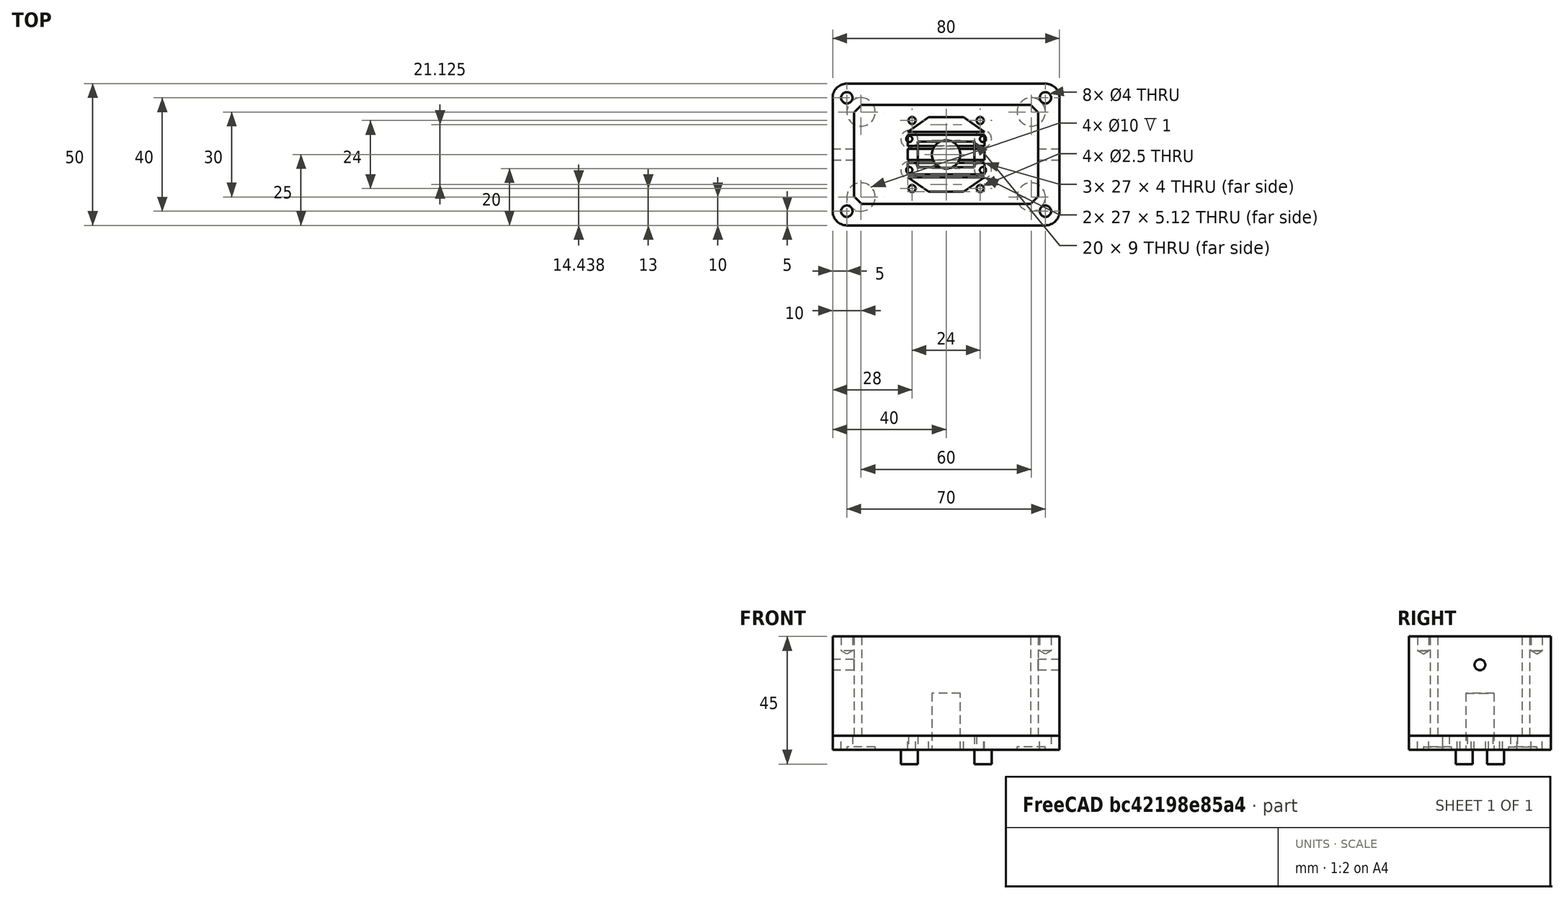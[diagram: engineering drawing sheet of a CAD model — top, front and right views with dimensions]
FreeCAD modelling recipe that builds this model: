
FCSTD DOCUMENT  (FreeCAD 0.20R29177 (Git))
Label: charger-box
License: All rights reserved
LicenseURL: http://en.wikipedia.org/wiki/All_rights_reserved
objects: Sketcher::SketchObject×11, PartDesign::Pocket×6, PartDesign::Pad×4, PartDesign::Body×3, App::Part×3, Mesh::Feature×3, PartDesign::Hole×1
note: 36 computed .brp shape members not serialized (recipe doc carries the construction recipe); baked Part::Feature solids carry a one-line shape summary decoded from their .brp

FEATURE [Sketcher::SketchObject] Sketch  label="box"
  FullyConstrained = true
  MapMode = 5
  Support = -> [XY_Plane]
  sketch-geometry (12):
    g0: ArcOfCircle CenterX=-35 CenterY=20 CenterZ=0 NormalX=0 NormalY=0 NormalZ=1 AngleXU=0 Radius=5 StartAngle=1.5708 EndAngle=3.14159
    g1: ArcOfCircle CenterX=-35 CenterY=-20 CenterZ=0 NormalX=0 NormalY=0 NormalZ=1 AngleXU=0 Radius=5 StartAngle=3.14159 EndAngle=4.71239
    g2: ArcOfCircle CenterX=35 CenterY=-20 CenterZ=0 NormalX=0 NormalY=0 NormalZ=1 AngleXU=0 Radius=5 StartAngle=4.71239 EndAngle=6.28319
    g3: ArcOfCircle CenterX=35 CenterY=20 CenterZ=0 NormalX=0 NormalY=0 NormalZ=1 AngleXU=0 Radius=5 StartAngle=3.97e-14 EndAngle=1.5708
    g4: LineSegment StartX=-35 StartY=25 StartZ=0 EndX=35 EndY=25 EndZ=0
    g5: LineSegment StartX=40 StartY=20 StartZ=0 EndX=40 EndY=-20 EndZ=0
    g6: LineSegment StartX=35 StartY=-25 StartZ=0 EndX=-35 EndY=-25 EndZ=0
    g7: LineSegment StartX=-40 StartY=-20 StartZ=0 EndX=-40 EndY=20 EndZ=0
    g8: LineSegment StartX=-35 StartY=20 StartZ=0 EndX=0 EndY=0 EndZ=0
    g9: LineSegment StartX=0 StartY=0 StartZ=0 EndX=35 EndY=-20 EndZ=0
    g10: LineSegment StartX=35 StartY=20 StartZ=0 EndX=0 EndY=0 EndZ=0
    g11: LineSegment StartX=0 StartY=0 StartZ=0 EndX=-35 EndY=-20 EndZ=0
  constraints (28):
    c: Diameter(g0) = 10
    c: Diameter(g3) = 10
    c: DistanceX(g0,g3) = 80
    c: DistanceY(g2,g3) = 50
    c: Horizontal(g4)
    c: Vertical(g5)
    c: Horizontal(g6)
    c: Vertical(g7)
    c: Equal(g4,g6)
    c: Equal(g7,g5)
    c: Tangent(g4,g0) = 1.5708
    c: Tangent(g4,g3) = 1.5708
    c: Tangent(g5,g3) = 1.5708
    c: Tangent(g5,g2) = 1.5708
    c: Tangent(g6,g2) = 1.5708
    c: Tangent(g6,g1) = 1.5708
    c: Tangent(g7,g1) = 1.5708
    c: Tangent(g7,g0) = 1.5708
    c: Coincident(g8,g0)
    c: Coincident(g8,g-1)
    c: Coincident(g9,g8)
    c: Coincident(g9,g2)
    c: Coincident(g10,g3)
    c: Coincident(g10,g8)
    c: Coincident(g11,g8)
    c: Coincident(g11,g1)
    c: Equal(g8,g9)
    c: Equal(g10,g11)
FEATURE [PartDesign::Pad] Pad
  Direction = (0,0,1)
  Length = 40
  Length2 = 10
  Profile = -> Sketch
  ReferenceAxis = -> Sketch [N_Axis]
  Type = 0
FEATURE [Sketcher::SketchObject] Sketch001  label="boxpocket"
  FullyConstrained = false
  MapMode = 5
  Placement = pos=(0,0,40) rot=(0,0,1;0rad)
  Support = -> [Pad]
  sketch-geometry (12):
    g0: LineSegment StartX=-32.5 StartY=14.8254 StartZ=0 EndX=-29.8254 EndY=17.5 EndZ=0
    g1: LineSegment StartX=-29.8254 StartY=17.5 StartZ=0 EndX=29.8254 EndY=17.5 EndZ=0
    g2: LineSegment StartX=29.8254 StartY=17.5 StartZ=0 EndX=32.5 EndY=14.8254 EndZ=0
    g3: LineSegment StartX=32.5 StartY=14.8254 StartZ=0 EndX=32.5 EndY=-14.8254 EndZ=0
    g4: LineSegment StartX=32.5 StartY=-14.8254 StartZ=0 EndX=29.8254 EndY=-17.5 EndZ=0
    g5: LineSegment StartX=29.8254 StartY=-17.5 StartZ=0 EndX=-29.8254 EndY=-17.5 EndZ=0
    g6: LineSegment StartX=-29.8254 StartY=-17.5 StartZ=0 EndX=-32.5 EndY=-14.8254 EndZ=0
    g7: LineSegment StartX=-32.5 StartY=-14.8254 StartZ=0 EndX=-32.5 EndY=14.8254 EndZ=0
    g8: LineSegment StartX=-32.5 StartY=14.8254 StartZ=0 EndX=0 EndY=0 EndZ=0
    g9: LineSegment StartX=0 StartY=0 StartZ=0 EndX=32.5 EndY=-14.8254 EndZ=0
    g10: LineSegment StartX=-32.5 StartY=-14.8254 StartZ=0 EndX=0 EndY=0 EndZ=0
    g11: LineSegment StartX=0 StartY=0 StartZ=0 EndX=32.5 EndY=14.8254 EndZ=0
  constraints (31):
    c: Coincident(g0,g1)
    c: Horizontal(g1)
    c: Coincident(g1,g2)
    c: Coincident(g2,g3)
    c: Vertical(g3)
    c: Coincident(g3,g4)
    c: Coincident(g4,g5)
    c: Horizontal(g5)
    c: Coincident(g5,g6)
    c: Coincident(g6,g7)
    c: Coincident(g7,g0)
    c: Vertical(g7)
    c: Equal(g1,g5)
    c: Equal(g7,g3)
    c: Equal(g0,g4)
    c: Equal(g2,g6)
    c: Equal(g6,g4)
    c: Angle(g7,g0) = 2.35619
    c: Angle(g2,g3) = 2.35619
    c: DistanceY(g4,g1) = 35
    c: DistanceX(g0,g2) = 65
    c: Coincident(g8,g0)
    c: Coincident(g8,g-1)
    c: Coincident(g9,g8)
    c: Coincident(g9,g3)
    c: Coincident(g10,g6)
    c: Coincident(g10,g8)
    c: Coincident(g11,g8)
    c: Coincident(g11,g2)
    c: Equal(g8,g9)
    c: Equal(g10,g11)
FEATURE [PartDesign::Pocket] Pocket
  BaseFeature = -> Pad
  Direction = (0,0,-1)
  Length = 35
  Length2 = 5
  Profile = -> Sketch001
  ReferenceAxis = -> Sketch001 [N_Axis]
  Type = 0
FEATURE [Sketcher::SketchObject] Sketch002  label="out vents sketch"
  FullyConstrained = true
  MapMode = 5
  Placement = pos=(0,0,0) rot=(1,0,0;3.14159rad)
  Support = -> [Pocket]
  sketch-geometry (32):
    g0: Circle CenterX=-12 CenterY=12 CenterZ=0 NormalX=0 NormalY=0 NormalZ=1 AngleXU=0 Radius=1.25
    g1: Circle CenterX=12 CenterY=12 CenterZ=0 NormalX=0 NormalY=0 NormalZ=1 AngleXU=0 Radius=1.25
    g2: Circle CenterX=-12 CenterY=-12 CenterZ=0 NormalX=0 NormalY=0 NormalZ=1 AngleXU=0 Radius=1.25
    g3: Circle CenterX=12 CenterY=-12 CenterZ=0 NormalX=0 NormalY=0 NormalZ=1 AngleXU=0 Radius=1.25
    g4: LineSegment StartX=-12 StartY=12 StartZ=0 EndX=12 EndY=12 EndZ=0
    g5: LineSegment StartX=12 StartY=-12 StartZ=0 EndX=12 EndY=12 EndZ=0
    g6: LineSegment StartX=12 StartY=-12 StartZ=0 EndX=-12 EndY=-12 EndZ=0
    g7: LineSegment StartX=-12 StartY=-12 StartZ=0 EndX=-12 EndY=12 EndZ=0
    g8: LineSegment StartX=-12 StartY=12 StartZ=0 EndX=0 EndY=0 EndZ=0
    g9: LineSegment StartX=0 StartY=0 StartZ=0 EndX=12 EndY=-12 EndZ=0
    g10: LineSegment StartX=12 StartY=12 StartZ=0 EndX=0 EndY=0 EndZ=0
    g11: LineSegment StartX=0 StartY=0 StartZ=0 EndX=-12 EndY=-12 EndZ=0
    g12: LineSegment StartX=-13.5 StartY=2 StartZ=0 EndX=13.5 EndY=2 EndZ=0
    g13: LineSegment StartX=13.5 StartY=2 StartZ=0 EndX=13.5 EndY=-2 EndZ=0
    g14: LineSegment StartX=13.5 StartY=-2 StartZ=0 EndX=-13.5 EndY=-2 EndZ=0
    g15: LineSegment StartX=-13.5 StartY=-2 StartZ=0 EndX=-13.5 EndY=2 EndZ=0
    g16: LineSegment StartX=-13.5 StartY=7 StartZ=0 EndX=13.5 EndY=7 EndZ=0
    g17: LineSegment StartX=-13.5 StartY=3 StartZ=0 EndX=-13.5 EndY=7 EndZ=0
    g18: LineSegment StartX=13.5 StartY=3 StartZ=0 EndX=-13.5 EndY=3 EndZ=0
    g19: LineSegment StartX=13.5 StartY=7 StartZ=0 EndX=13.5 EndY=3 EndZ=0
    g20: LineSegment StartX=-13.5 StartY=-7 StartZ=0 EndX=-13.5 EndY=-3 EndZ=0
    g21: LineSegment StartX=-13.5 StartY=-3 StartZ=0 EndX=13.5 EndY=-3 EndZ=0
    g22: LineSegment StartX=13.5 StartY=-3 StartZ=0 EndX=13.5 EndY=-7 EndZ=0
    g23: LineSegment StartX=13.5 StartY=-7 StartZ=0 EndX=-13.5 EndY=-7 EndZ=0
    g24: LineSegment StartX=-13.5 StartY=8 StartZ=0 EndX=-6.18074 EndY=13.125 EndZ=0
    g25: LineSegment StartX=-6.18074 StartY=13.125 StartZ=0 EndX=6.18074 EndY=13.125 EndZ=0
    g26: LineSegment StartX=6.18074 StartY=13.125 StartZ=0 EndX=13.5 EndY=8 EndZ=0
    g27: LineSegment StartX=13.5 StartY=8 StartZ=0 EndX=-13.5 EndY=8 EndZ=0
    g28: LineSegment StartX=-13.5 StartY=-8 StartZ=0 EndX=13.5 EndY=-8 EndZ=0
    g29: LineSegment StartX=13.5 StartY=-8 StartZ=0 EndX=6.18074 EndY=-13.125 EndZ=0
    g30: LineSegment StartX=6.18074 StartY=-13.125 StartZ=0 EndX=-6.18074 EndY=-13.125 EndZ=0
    g31: LineSegment StartX=-6.18074 StartY=-13.125 StartZ=0 EndX=-13.5 EndY=-8 EndZ=0
  constraints (86):
    c: Diameter(g0) = 2.5
    c: Diameter(g1) = 2.5
    c: Diameter(g3) = 2.5
    c: Diameter(g2) = 2.5
    c: Coincident(g4,g0)
    c: Coincident(g4,g1)
    c: Horizontal(g4)
    c: Coincident(g5,g3)
    c: Coincident(g5,g1)
    c: Coincident(g6,g3)
    c: Coincident(g6,g2)
    c: Coincident(g7,g2)
    c: Coincident(g7,g0)
    c: Vertical(g7)
    c: Perpendicular(g4,g5)
    c: Perpendicular(g5,g6)
    c: Coincident(g8,g0)
    c: Coincident(g9,g8)
    c: Coincident(g9,g3)
    c: Coincident(g10,g1)
    c: Coincident(g10,g8)
    c: Coincident(g11,g8)
    c: Coincident(g11,g2)
    c: Equal(g8,g9)
    c: Equal(g10,g11)
    c: DistanceX(g4,g4) = 24
    c: DistanceY(g5,g5) = 24
    c: Coincident(g8,g-1)
    c: Coincident(g12,g13)
    c: Coincident(g13,g14)
    c: Coincident(g14,g15)
    c: Coincident(g15,g12)
    c: Horizontal(g12)
    c: Horizontal(g14)
    c: Vertical(g13)
    c: Vertical(g15)
    c: DistanceX(g12,g12) = 27
    c: DistanceY(g15,g15) = 4
    c: DistanceY(g8,g12) = 2
    c: DistanceX(g12,g8) = 13.5
    c: Coincident(g16,g19)
    c: Coincident(g19,g18)
    c: Coincident(g18,g17)
    c: Coincident(g17,g16)
    c: Horizontal(g16)
    c: Horizontal(g18)
    c: Vertical(g19)
    c: Vertical(g17)
    c: DistanceX(g16,g16) = 27
    c: DistanceY(g17,g17) = 4
    c: DistanceY(g12,g17) = 1
    c: DistanceX(g16,g8) = 13.5
    c: Coincident(g21,g22)
    c: Coincident(g22,g23)
    c: Coincident(g23,g20)
    c: Coincident(g20,g21)
    c: Horizontal(g21)
    c: Horizontal(g23)
    c: Vertical(g22)
    c: Vertical(g20)
    c: DistanceX(g21,g21) = 27
    c: DistanceY(g20,g20) = 4
    c: DistanceY(g20,g14) = 1
    c: DistanceX(g20,g8) = 13.5
    c: Coincident(g24,g25)
    c: Coincident(g25,g26)
    c: Coincident(g26,g27)
    c: Coincident(g27,g24)
    c: Horizontal(g27)
    c: Angle(g27,g24) = 0.610865
    c: Angle(g26,g27) = 0.610865
    c: DistanceX(g24,g26) = 27
    c: Coincident(g28,g29)
    c: Coincident(g29,g30)
    c: Horizontal(g30)
    c: Coincident(g30,g31)
    c: Coincident(g31,g28)
    c: Angle(g31,g28) = 0.610865
    c: Angle(g28,g29) = 0.610865
    c: DistanceY(g29,g28) = 5.125
    c: DistanceX(g28,g28) = 27
    c: Symmetric(g24,g25,g-2)
    c: DistanceY(g16,g24) = 1
    c: DistanceY(g24,g24) = 5.125
    c: Symmetric(g28,g28,g-2)
    c: DistanceY(g28,g20) = 1
FEATURE [PartDesign::Pocket] Pocket001  label="out vents"
  BaseFeature = -> Pocket
  Direction = (0,0,1)
  Length = 10
  Length2 = 5
  Profile = -> Sketch002
  ReferenceAxis = -> Sketch002 [N_Axis]
  Type = 0
FEATURE [Sketcher::SketchObject] Sketch003  label="topholes"
  FullyConstrained = true
  MapMode = 5
  Placement = pos=(0,0,40) rot=(0,0,1;0rad)
  Support = -> [Pocket001]
  sketch-geometry (12):
    g0: Circle CenterX=-35 CenterY=20 CenterZ=0 NormalX=0 NormalY=0 NormalZ=1 AngleXU=0 Radius=2
    g1: Circle CenterX=35 CenterY=20 CenterZ=0 NormalX=0 NormalY=0 NormalZ=1 AngleXU=0 Radius=2
    g2: Circle CenterX=35 CenterY=-20 CenterZ=0 NormalX=0 NormalY=0 NormalZ=1 AngleXU=0 Radius=2
    g3: Circle CenterX=-35 CenterY=-20 CenterZ=0 NormalX=0 NormalY=0 NormalZ=1 AngleXU=0 Radius=2
    g4: LineSegment StartX=-35 StartY=20 StartZ=0 EndX=-35 EndY=-20 EndZ=0
    g5: LineSegment StartX=-35 StartY=-20 StartZ=0 EndX=35 EndY=-20 EndZ=0
    g6: LineSegment StartX=35 StartY=-20 StartZ=0 EndX=35 EndY=20 EndZ=0
    g7: LineSegment StartX=35 StartY=20 StartZ=0 EndX=-35 EndY=20 EndZ=0
    g8: LineSegment StartX=-35 StartY=20 StartZ=0 EndX=0 EndY=0 EndZ=0
    g9: LineSegment StartX=0 StartY=0 StartZ=0 EndX=35 EndY=-20 EndZ=0
    g10: LineSegment StartX=35 StartY=20 StartZ=0 EndX=0 EndY=0 EndZ=0
    g11: LineSegment StartX=0 StartY=0 StartZ=0 EndX=-35 EndY=-20 EndZ=0
  constraints (28):
    c: Coincident(g4,g0)
    c: Coincident(g4,g3)
    c: Vertical(g4)
    c: Coincident(g5,g3)
    c: Coincident(g5,g2)
    c: Horizontal(g5)
    c: Coincident(g6,g2)
    c: Coincident(g6,g1)
    c: Vertical(g6)
    c: Coincident(g7,g1)
    c: Coincident(g7,g0)
    c: Horizontal(g7)
    c: Diameter(g0) = 4
    c: Diameter(g1) = 4
    c: Diameter(g2) = 4
    c: Diameter(g3) = 4
    c: Coincident(g8,g0)
    c: Coincident(g8,g-1)
    c: Coincident(g9,g8)
    c: Coincident(g9,g2)
    c: Coincident(g10,g1)
    c: Coincident(g10,g8)
    c: Coincident(g11,g8)
    c: Coincident(g11,g3)
    c: Equal(g11,g10)
    c: Equal(g8,g9)
    c: DistanceX(g7,g7) = 70
    c: DistanceY(g4,g4) = 40
FEATURE [PartDesign::Hole] Hole  label="top holes hole"
  BaseFeature = -> Pocket001
  CustomThreadClearance = 0
  Depth = 5
  DepthType = 0
  Diameter = 4
  DrillForDepth = false
  DrillPoint = 1
  DrillPointAngle = 118
  HoleCutCountersinkAngle = 90
  HoleCutCustomValues = false
  HoleCutDepth = 0
  HoleCutDiameter = 6.1
  HoleCutType = 0
  ModelThread = false
  Profile = -> Sketch003
  Tapered = false
  TaperedAngle = 90
  ThreadClass = 0
  ThreadDepth = 5
  ThreadDepthType = 0
  ThreadDirection = 0
  ThreadFit = 0
  ThreadSize = 0
  ThreadType = 0
  Threaded = false
  UseCustomThreadClearance = false
FEATURE [Sketcher::SketchObject] Sketch004  label="botholes"
  FullyConstrained = true
  MapMode = 5
  Placement = pos=(0,0,0) rot=(1,0,0;3.14159rad)
  Support = -> [Hole]
  sketch-geometry (4):
    g0: Circle CenterX=-30 CenterY=15 CenterZ=0 NormalX=0 NormalY=0 NormalZ=1 AngleXU=0 Radius=5
    g1: Circle CenterX=-30 CenterY=-15 CenterZ=0 NormalX=0 NormalY=0 NormalZ=1 AngleXU=0 Radius=5
    g2: Circle CenterX=30 CenterY=15 CenterZ=0 NormalX=0 NormalY=0 NormalZ=1 AngleXU=0 Radius=5
    g3: Circle CenterX=30 CenterY=-15 CenterZ=0 NormalX=0 NormalY=0 NormalZ=1 AngleXU=0 Radius=5
  constraints (9):
    c: Diameter(g0) = 10
    c: Diameter(g1) = 10
    c: Symmetric(g0,g1,g-1)
    c: Diameter(g2) = 10
    c: Diameter(g3) = 10
    c: Symmetric(g0,g2,g-2)
    c: Symmetric(g1,g3,g-2)
    c: DistanceX(g1,g-1) = 30
    c: DistanceY(g1,g-1) = 15
FEATURE [PartDesign::Pocket] Pocket002  label="bottom holes pocket"
  BaseFeature = -> Hole
  Direction = (0,0,1)
  Length = 1
  Length2 = 5
  Profile = -> Sketch004
  ReferenceAxis = -> Sketch004 [N_Axis]
  Type = 0
FEATURE [Sketcher::SketchObject] Sketch005  label="lid sketch"
  FullyConstrained = true
  MapMode = 5
  Support = -> [XY_Plane003]
  sketch-geometry (12):
    g0: ArcOfCircle CenterX=-35 CenterY=20 CenterZ=0 NormalX=0 NormalY=0 NormalZ=1 AngleXU=0 Radius=5 StartAngle=1.5708 EndAngle=3.14159
    g1: ArcOfCircle CenterX=-35 CenterY=-20 CenterZ=0 NormalX=0 NormalY=0 NormalZ=1 AngleXU=0 Radius=5 StartAngle=3.14159 EndAngle=4.71239
    g2: ArcOfCircle CenterX=35 CenterY=-20 CenterZ=0 NormalX=0 NormalY=0 NormalZ=1 AngleXU=0 Radius=5 StartAngle=4.71239 EndAngle=6.28319
    g3: ArcOfCircle CenterX=35 CenterY=20 CenterZ=0 NormalX=0 NormalY=0 NormalZ=1 AngleXU=0 Radius=5 StartAngle=3.97e-14 EndAngle=1.5708
    g4: LineSegment StartX=-35 StartY=25 StartZ=0 EndX=35 EndY=25 EndZ=0
    g5: LineSegment StartX=40 StartY=20 StartZ=0 EndX=40 EndY=-20 EndZ=0
    g6: LineSegment StartX=35 StartY=-25 StartZ=0 EndX=-35 EndY=-25 EndZ=0
    g7: LineSegment StartX=-40 StartY=-20 StartZ=0 EndX=-40 EndY=20 EndZ=0
    g8: LineSegment StartX=-35 StartY=20 StartZ=0 EndX=0 EndY=0 EndZ=0
    g9: LineSegment StartX=0 StartY=0 StartZ=0 EndX=35 EndY=-20 EndZ=0
    g10: LineSegment StartX=35 StartY=20 StartZ=0 EndX=0 EndY=0 EndZ=0
    g11: LineSegment StartX=0 StartY=0 StartZ=0 EndX=-35 EndY=-20 EndZ=0
  constraints (28):
    c: Diameter(g0) = 10
    c: Diameter(g3) = 10
    c: DistanceX(g0,g3) = 80
    c: DistanceY(g2,g3) = 50
    c: Horizontal(g4)
    c: Vertical(g5)
    c: Horizontal(g6)
    c: Vertical(g7)
    c: Equal(g4,g6)
    c: Equal(g7,g5)
    c: Tangent(g4,g0) = 1.5708
    c: Tangent(g4,g3) = 1.5708
    c: Tangent(g5,g3) = 1.5708
    c: Tangent(g5,g2) = 1.5708
    c: Tangent(g6,g2) = 1.5708
    c: Tangent(g6,g1) = 1.5708
    c: Tangent(g7,g1) = 1.5708
    c: Tangent(g7,g0) = 1.5708
    c: Coincident(g8,g0)
    c: Coincident(g8,g-1)
    c: Coincident(g9,g8)
    c: Coincident(g9,g2)
    c: Coincident(g10,g3)
    c: Coincident(g10,g8)
    c: Coincident(g11,g8)
    c: Coincident(g11,g1)
    c: Equal(g8,g9)
    c: Equal(g10,g11)
FEATURE [PartDesign::Pad] Pad001  label="lid pad"
  Direction = (0,0,1)
  Length = 5
  Length2 = 10
  Profile = -> Sketch005
  ReferenceAxis = -> Sketch005 [N_Axis]
  Type = 0
FEATURE [Sketcher::SketchObject] Sketch006  label="holes"
  FullyConstrained = true
  MapMode = 5
  Placement = pos=(0,0,5) rot=(0,0,1;0rad)
  Support = -> [Pad001]
  sketch-geometry (4):
    g0: Circle CenterX=-35 CenterY=20 CenterZ=0 NormalX=0 NormalY=0 NormalZ=1 AngleXU=0 Radius=2
    g1: Circle CenterX=35 CenterY=20 CenterZ=0 NormalX=0 NormalY=0 NormalZ=1 AngleXU=0 Radius=2
    g2: Circle CenterX=35 CenterY=-20 CenterZ=0 NormalX=0 NormalY=0 NormalZ=1 AngleXU=0 Radius=2
    g3: Circle CenterX=-35 CenterY=-20 CenterZ=0 NormalX=0 NormalY=0 NormalZ=1 AngleXU=0 Radius=2
  constraints (9):
    c: Diameter(g0) = 4
    c: Diameter(g1) = 4
    c: Diameter(g2) = 4
    c: Diameter(g3) = 4
    c: Symmetric(g0,g1,g-2)
    c: Symmetric(g3,g2,g-2)
    c: Symmetric(g0,g3,g-1)
    c: DistanceX(g0,g1) = 70
    c: DistanceY(g3,g0) = 40
FEATURE [PartDesign::Pocket] Pocket003  label="lid with holes"
  BaseFeature = -> Pad001
  Direction = (0,0,-1)
  Length = 20
  Length2 = 5
  Profile = -> Sketch006
  ReferenceAxis = -> Sketch006 [N_Axis]
  Type = 0
FEATURE [Sketcher::SketchObject] Sketch007  label="pcb holes and front intake"
  FullyConstrained = true
  MapMode = 5
  Placement = pos=(0,0,5) rot=(0,0,1;0rad)
  Support = -> [Pocket003]
  sketch-geometry (8):
    g0: Circle CenterX=-13 CenterY=5.5 CenterZ=0 NormalX=0 NormalY=0 NormalZ=1 AngleXU=0 Radius=1.1
    g1: Circle CenterX=13 CenterY=5.5 CenterZ=0 NormalX=0 NormalY=0 NormalZ=1 AngleXU=0 Radius=1.1
    g2: Circle CenterX=13 CenterY=-5.5 CenterZ=0 NormalX=0 NormalY=0 NormalZ=1 AngleXU=0 Radius=1.1
    g3: Circle CenterX=-13 CenterY=-5.5 CenterZ=0 NormalX=0 NormalY=0 NormalZ=1 AngleXU=0 Radius=1.1
    g4: LineSegment StartX=-10 StartY=4.5 StartZ=0 EndX=10 EndY=4.5 EndZ=0
    g5: LineSegment StartX=10 StartY=4.5 StartZ=0 EndX=10 EndY=-4.5 EndZ=0
    g6: LineSegment StartX=10 StartY=-4.5 StartZ=0 EndX=-10 EndY=-4.5 EndZ=0
    g7: LineSegment StartX=-10 StartY=-4.5 StartZ=0 EndX=-10 EndY=4.5 EndZ=0
  constraints (19):
    c: Diameter(g0) = 2.2
    c: Diameter(g1) = 2.2
    c: Diameter(g2) = 2.2
    c: Diameter(g3) = 2.2
    c: Symmetric(g0,g1,g-2)
    c: Symmetric(g2,g3,g-2)
    c: Symmetric(g0,g3,g-1)
    c: DistanceX(g0,g1) = 26
    c: DistanceY(g3,g0) = 11
    c: Coincident(g4,g5)
    c: Coincident(g5,g6)
    c: Coincident(g6,g7)
    c: Coincident(g7,g4)
    c: Horizontal(g6)
    c: Vertical(g5)
    c: Symmetric(g4,g4,g-2)
    c: Symmetric(g4,g6,g-1)
    c: DistanceX(g4,g4) = 20
    c: DistanceY(g6,g4) = 9
FEATURE [Sketcher::SketchObject] Sketch008  label="pillars"
  FullyConstrained = true
  MapMode = 5
  Placement = pos=(0,0,0) rot=(1,0,0;3.14159rad)
  sketch-geometry (4):
    g0: Circle CenterX=-13 CenterY=5.5 CenterZ=0 NormalX=0 NormalY=0 NormalZ=1 AngleXU=0 Radius=3
    g1: Circle CenterX=13 CenterY=5.5 CenterZ=0 NormalX=0 NormalY=0 NormalZ=1 AngleXU=0 Radius=3
    g2: Circle CenterX=13 CenterY=-5.5 CenterZ=0 NormalX=0 NormalY=0 NormalZ=1 AngleXU=0 Radius=3
    g3: Circle CenterX=-13 CenterY=-5.5 CenterZ=0 NormalX=0 NormalY=0 NormalZ=1 AngleXU=0 Radius=3
  constraints (9):
    c: Diameter(g0) = 6
    c: Diameter(g1) = 6
    c: Diameter(g2) = 6
    c: Diameter(g3) = 6
    c: Symmetric(g0,g3,g-1)
    c: Symmetric(g1,g2,g-1)
    c: Symmetric(g0,g1,g-2)
    c: DistanceX(g0,g1) = 26
    c: DistanceY(g3,g0) = 11
FEATURE [PartDesign::Pad] Pad002  label="lid with pillars"
  BaseFeature = -> Pocket003
  Direction = (0,0,-1)
  Length = 5
  Length2 = 10
  Profile = -> Sketch008
  ReferenceAxis = -> Sketch008 [N_Axis]
  Type = 0
FEATURE [PartDesign::Pocket] Pocket004  label="lid with intake and pcb holes"
  BaseFeature = -> Pad002
  Direction = (0,0,-1)
  Length = 20
  Length2 = 5
  Profile = -> Sketch007
  ReferenceAxis = -> Sketch007 [N_Axis]
  Type = 0
FEATURE [PartDesign::Body] Body001  label="lid body"
  Group = -> [Sketch005,Pad001,Sketch006,Pocket003,Sketch007,Sketch008,Pad002,Pocket004]
  Origin = -> Origin003
  Tip = -> Pocket004
FEATURE [App::Part] Part  label="lid"
  Group = -> [Body001]
  Origin = -> Origin001
FEATURE [Sketcher::SketchObject] Sketch009  label="cable holes"
  FullyConstrained = true
  MapMode = 5
  Placement = pos=(-40,0,0) rot=(0.57735,-0.57735,-0.57735;2.0944rad)
  Support = -> [Hole]
  sketch-geometry (1):
    g0: Circle CenterX=0 CenterY=30 CenterZ=0 NormalX=0 NormalY=0 NormalZ=1 AngleXU=0 Radius=1.9
  constraints (3):
    c: PointOnObject(g0,g-2)
    c: Diameter(g0) = 3.8
    c: DistanceY(g-1,g0) = 30
FEATURE [PartDesign::Pocket] Pocket005  label="side holes pocket"
  BaseFeature = -> Pocket002
  Direction = (1,0,0)
  Length = 100
  Length2 = 5
  Profile = -> Sketch009
  ReferenceAxis = -> Sketch009 [N_Axis]
  Type = 0
FEATURE [PartDesign::Body] Body
  Group = -> [Sketch,Pad,Sketch001,Pocket,Sketch002,Pocket001,Sketch003,Hole,Sketch004,Pocket002,Sketch009,Pocket005]
  Origin = -> Origin
  Tip = -> Pocket005
FEATURE [App::Part] Part001  label="body"
  Group = -> [Body]
  Origin = -> Origin002
FEATURE [Mesh::Feature] Mesh  label="body (Meshed)"
FEATURE [Mesh::Feature] Mesh001  label="lid (Meshed)"
  Placement = pos=(0,0,92) rot=(0,0,1;0rad)
FEATURE [Sketcher::SketchObject] Sketch010  label="leg sketch"
  FullyConstrained = true
  MapMode = 5
  Support = -> [XY_Plane005]
  sketch-geometry (1):
    g0: Circle CenterX=0 CenterY=0 CenterZ=0 NormalX=0 NormalY=0 NormalZ=1 AngleXU=0 Radius=5
  constraints (2):
    c: Coincident(g0,g-1)
    c: Diameter(g0) = 10
FEATURE [PartDesign::Pad] Pad003  label="padded leg"
  Direction = (0,0,1)
  Length = 20
  Length2 = 10
  Profile = -> Sketch010
  ReferenceAxis = -> Sketch010 [N_Axis]
  Type = 0
FEATURE [PartDesign::Body] Body002  label="leg body"
  Group = -> [Sketch010,Pad003]
  Origin = -> Origin005
  Tip = -> Pad003
FEATURE [App::Part] Part002  label="leg"
  Group = -> [Body002]
  Origin = -> Origin004
FEATURE [Mesh::Feature] Mesh002  label="leg (Meshed)"
